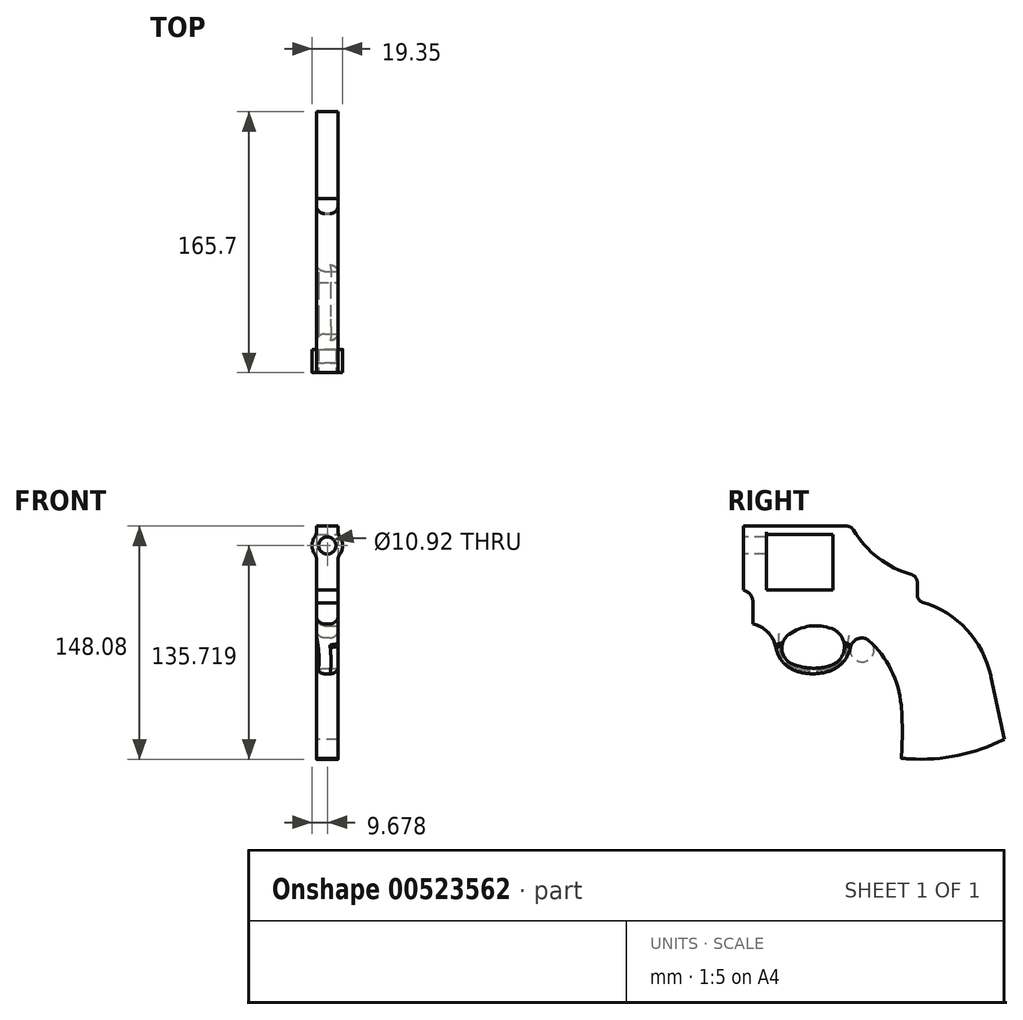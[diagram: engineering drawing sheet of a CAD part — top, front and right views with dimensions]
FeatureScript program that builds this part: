
annotation { "Feature Type Name" : "Feature", "Feature Type Description" : "" }
export const myFeature = defineFeature(function(context is Context, id is Id, definition is map)
    precondition{}
    {
        {
            var Q0;
            Q0=qCreatedBy(makeId("Right.planeOp"),FACE);
            var sketch = newSketch(context, id + "F0", { "sketchPlane" : qUnion([Q0])});
            skLineSegment(sketch, "E0", {"start": v(-44.54, 37.78) * mm, "end": v(-44.54, -2.86) * mm});
            skLineSegment(sketch, "E1", {"start": v(-44.54, 37.78) * mm, "end": v(24.04, 37.78) * mm});
            skLineSegment(sketch, "E2", {"start": v(-51.95, 6.03) * mm, "end": v(65.95, 6.03) * mm, "construction": true});
            skArc(sketch, "E3", {"start": v(24.04, 37.78) * mm, "mid": v(41.55, 17.35) * mm, "end": v(65.95, 6.03) * mm});
            skArc(sketch, "E4", {"start": v(-38.5, -10.9) * mm, "mid": v(-40.03, -5.77) * mm, "end": v(-44.54, -2.86) * mm});
            skLineSegment(sketch, "E5", {"start": v(-38.5, -10.9) * mm, "end": v(-38.5, -24.32) * mm});
            skArc(sketch, "E6", {"start": v(-23.87, -39.34) * mm, "mid": v(-28.94, -29.64) * mm, "end": v(-38.5, -24.32) * mm});
            skArc(sketch, "E7", {"start": v(-23.87, -39.34) * mm, "mid": v(-19.25, -48.7) * mm, "end": v(-10.5, -54.4) * mm});
            skArc(sketch, "E8", {"start": v(-10.5, -54.4) * mm, "mid": v(-0.28, -56) * mm, "end": v(9.93, -54.4) * mm});
            skArc(sketch, "E9", {"start": v(9.93, -54.4) * mm, "mid": v(18.76, -48.7) * mm, "end": v(23.5, -39.34) * mm});
            skArc(sketch, "E10", {"start": v(31.68, -33.31) * mm, "mid": v(26.44, -34.76) * mm, "end": v(23.5, -39.34) * mm});
            skArc(sketch, "E11", {"start": v(35, -34.76) * mm, "mid": v(33.46, -33.77) * mm, "end": v(31.68, -33.31) * mm});
            skPoint(sketch, "E11.startSnap0", {"position": v(26.44, -34.76) * mm});
            skArc(sketch, "E12", {"start": v(112.83, -58.17) * mm, "mid": v(112.72, -57.65) * mm, "end": v(112.6, -57.14) * mm});
            skArc(sketch, "E13", {"start": v(55.75, -109.63) * mm, "mid": v(89.3, -108.4) * mm, "end": v(121.16, -97.73) * mm});
            skArc(sketch, "E14", {"start": v(55.75, -109.63) * mm, "mid": v(56.47, -92.87) * mm, "end": v(55.75, -76.1) * mm});
            skArc(sketch, "E15", {"start": v(55.75, -76.1) * mm, "mid": v(49.34, -53.44) * mm, "end": v(35, -34.76) * mm});
            skLineSegment(sketch, "E16", {"start": v(112.83, -58.17) * mm, "end": v(121.16, -97.73) * mm});
            skLineSegment(sketch, "E17", {"start": v(65.95, 6.03) * mm, "end": v(65.95, -9.62) * mm});
            skArc(sketch, "E18", {"start": v(112.6, -57.14) * mm, "mid": v(96.09, -26.7) * mm, "end": v(65.95, -9.62) * mm});
            skSolve(sketch);
        }
        {
            var Q0;
            Q0 = qSketchRegion(id + "F0", true);
            extrude(context, id + "F1", {"entities" : qUnion([Q0]), "depth" : 13.72 * mm, "offsetDistance" : 25.4 * mm});
        }
        {
            var Q0;
            Q0=makeQuery(id+"F1.opExtrude","CAP_FACE",FACE,{"disambiguationData":[OSD([sQuery(id+"F0.wireOp",EDGE,"E0"),sQuery(id+"F0.wireOp",EDGE,"E1"),sQuery(id+"F0.wireOp",EDGE,"E3"),sQuery(id+"F0.wireOp",EDGE,"E4"),sQuery(id+"F0.wireOp",EDGE,"E5"),sQuery(id+"F0.wireOp",EDGE,"E6"),sQuery(id+"F0.wireOp",EDGE,"E7"),sQuery(id+"F0.wireOp",EDGE,"E8"),sQuery(id+"F0.wireOp",EDGE,"E9"),sQuery(id+"F0.wireOp",EDGE,"E10"),sQuery(id+"F0.wireOp",EDGE,"E11"),sQuery(id+"F0.wireOp",EDGE,"E12"),sQuery(id+"F0.wireOp",EDGE,"E13"),sQuery(id+"F0.wireOp",EDGE,"E14"),sQuery(id+"F0.wireOp",EDGE,"E15"),sQuery(id+"F0.wireOp",EDGE,"E16")])],"isStart":false});
            var sketch = newSketch(context, id + "F2", { "sketchPlane" : qUnion([Q0])});
            skLineSegment(sketch, "E19.bottom", {"start": v(-29.8, 32.52) * mm, "end": v(12.53, 32.52) * mm});
            skLineSegment(sketch, "E19.top", {"start": v(-29.8, -2.9) * mm, "end": v(12.53, -2.9) * mm});
            skLineSegment(sketch, "E19.left", {"start": v(-29.8, 32.52) * mm, "end": v(-29.8, -2.9) * mm});
            skLineSegment(sketch, "E19.right", {"start": v(12.53, 32.52) * mm, "end": v(12.53, -2.9) * mm});
            skSolve(sketch);
        }
        {
            var Q0;
            Q0 = qSketchRegion(id + "F2", true);
            extrude(context, id + "F3", {"entities" : qUnion([Q0]), "operationType" : NewBodyOperationType.REMOVE, "oppositeDirection" : true, "depth" : 25.4 * mm, "offsetDistance" : 25.4 * mm});
        }
        {
            var Q0;
            Q0=makeQuery(id+"F1.opExtrude","SWEPT_FACE",FACE,{"disambiguationData":[OSD([sQuery(id+"F0.wireOp",EDGE,"E0")])]});
            var sketch = newSketch(context, id + "F4", { "sketchPlane" : qUnion([Q0])});
            skLineSegment(sketch, "E20", {"start": v(6.86, 37.78) * mm, "end": v(6.86, 2.4) * mm, "construction": true});
            skPoint(sketch, "E20.endSnap0", {"position": v(6.86, 37.78) * mm});
            skSolve(sketch);
        }
        {
            var Q0;
            {var subQ0=sQuery(id+"F0.wireOp",EDGE,"E0");Q0=makeQuery(id+"F4.imprint","IMPRINT",FACE,{"disambiguationData":[TD([[makeQuery(id+"F4.imprint","IMPRINT",EDGE,{"derivedFrom":makeQuery(id+"F1.opExtrude","CAP_EDGE",EDGE,{"disambiguationData":[OSD([subQ0])],"isStart":true})}),1.0]])]});}
            var sketch = newSketch(context, id + "F5", { "sketchPlane" : qUnion([Q0])});
            skCircle(sketch, "E21", {"center": v(6.86, 25.48) * mm, "radius": 9.68 * mm});
            skSolve(sketch);
        }
        {
            var Q0;
            Q0 = qSketchRegion(id + "F5", true);
            extrude(context, id + "F6", {"entities" : qUnion([Q0]), "operationType" : NewBodyOperationType.ADD, "oppositeDirection" : true, "depth" : 14.73 * mm, "offsetDistance" : 25.4 * mm});
        }
        {
            var Q0;
            Q0=makeQuery(id+"F6.boolean.opBoolean","INTERSECT",EDGE,{"disambiguationData":[OD(0.0)],"derivedFrom":[makeQuery(id+"F1.opExtrude","CAP_FACE",FACE,{"disambiguationData":[OSD([sQuery(id+"F0.wireOp",EDGE,"E0"),sQuery(id+"F0.wireOp",EDGE,"E1"),sQuery(id+"F0.wireOp",EDGE,"E3"),sQuery(id+"F0.wireOp",EDGE,"E4"),sQuery(id+"F0.wireOp",EDGE,"E5"),sQuery(id+"F0.wireOp",EDGE,"E6"),sQuery(id+"F0.wireOp",EDGE,"E7"),sQuery(id+"F0.wireOp",EDGE,"E8"),sQuery(id+"F0.wireOp",EDGE,"E9"),sQuery(id+"F0.wireOp",EDGE,"E10"),sQuery(id+"F0.wireOp",EDGE,"E11"),sQuery(id+"F0.wireOp",EDGE,"E12"),sQuery(id+"F0.wireOp",EDGE,"E13"),sQuery(id+"F0.wireOp",EDGE,"E14"),sQuery(id+"F0.wireOp",EDGE,"E15"),sQuery(id+"F0.wireOp",EDGE,"E16")])],"isStart":false}),makeQuery(id+"F6.opExtrude","SWEPT_FACE",FACE,{"disambiguationData":[OSD([sQuery(id+"F5.wireOp",EDGE,"E21")])]})]});
            var Q1;
            Q1=makeQuery(id+"F6.boolean.opBoolean","INTERSECT",EDGE,{"disambiguationData":[OD(1.0)],"derivedFrom":[makeQuery(id+"F1.opExtrude","CAP_FACE",FACE,{"disambiguationData":[OSD([sQuery(id+"F0.wireOp",EDGE,"E0"),sQuery(id+"F0.wireOp",EDGE,"E1"),sQuery(id+"F0.wireOp",EDGE,"E3"),sQuery(id+"F0.wireOp",EDGE,"E4"),sQuery(id+"F0.wireOp",EDGE,"E5"),sQuery(id+"F0.wireOp",EDGE,"E6"),sQuery(id+"F0.wireOp",EDGE,"E7"),sQuery(id+"F0.wireOp",EDGE,"E8"),sQuery(id+"F0.wireOp",EDGE,"E9"),sQuery(id+"F0.wireOp",EDGE,"E10"),sQuery(id+"F0.wireOp",EDGE,"E11"),sQuery(id+"F0.wireOp",EDGE,"E12"),sQuery(id+"F0.wireOp",EDGE,"E13"),sQuery(id+"F0.wireOp",EDGE,"E14"),sQuery(id+"F0.wireOp",EDGE,"E15"),sQuery(id+"F0.wireOp",EDGE,"E16")])],"isStart":false}),makeQuery(id+"F6.opExtrude","SWEPT_FACE",FACE,{"disambiguationData":[OSD([sQuery(id+"F5.wireOp",EDGE,"E21")])]})]});
            var Q2;
            Q2=makeQuery(id+"F6.boolean.opBoolean","INTERSECT",EDGE,{"disambiguationData":[OD(1.0)],"derivedFrom":[makeQuery(id+"F1.opExtrude","CAP_FACE",FACE,{"disambiguationData":[OSD([sQuery(id+"F0.wireOp",EDGE,"E0"),sQuery(id+"F0.wireOp",EDGE,"E1"),sQuery(id+"F0.wireOp",EDGE,"E3"),sQuery(id+"F0.wireOp",EDGE,"E4"),sQuery(id+"F0.wireOp",EDGE,"E5"),sQuery(id+"F0.wireOp",EDGE,"E6"),sQuery(id+"F0.wireOp",EDGE,"E7"),sQuery(id+"F0.wireOp",EDGE,"E8"),sQuery(id+"F0.wireOp",EDGE,"E9"),sQuery(id+"F0.wireOp",EDGE,"E10"),sQuery(id+"F0.wireOp",EDGE,"E11"),sQuery(id+"F0.wireOp",EDGE,"E12"),sQuery(id+"F0.wireOp",EDGE,"E13"),sQuery(id+"F0.wireOp",EDGE,"E14"),sQuery(id+"F0.wireOp",EDGE,"E15"),sQuery(id+"F0.wireOp",EDGE,"E16")])],"isStart":true}),makeQuery(id+"F6.opExtrude","SWEPT_FACE",FACE,{"disambiguationData":[OSD([sQuery(id+"F5.wireOp",EDGE,"E21")])]})]});
            var Q3;
            Q3=makeQuery(id+"F6.boolean.opBoolean","INTERSECT",EDGE,{"disambiguationData":[OD(0.0)],"derivedFrom":[makeQuery(id+"F1.opExtrude","CAP_FACE",FACE,{"disambiguationData":[OSD([sQuery(id+"F0.wireOp",EDGE,"E0"),sQuery(id+"F0.wireOp",EDGE,"E1"),sQuery(id+"F0.wireOp",EDGE,"E3"),sQuery(id+"F0.wireOp",EDGE,"E4"),sQuery(id+"F0.wireOp",EDGE,"E5"),sQuery(id+"F0.wireOp",EDGE,"E6"),sQuery(id+"F0.wireOp",EDGE,"E7"),sQuery(id+"F0.wireOp",EDGE,"E8"),sQuery(id+"F0.wireOp",EDGE,"E9"),sQuery(id+"F0.wireOp",EDGE,"E10"),sQuery(id+"F0.wireOp",EDGE,"E11"),sQuery(id+"F0.wireOp",EDGE,"E12"),sQuery(id+"F0.wireOp",EDGE,"E13"),sQuery(id+"F0.wireOp",EDGE,"E14"),sQuery(id+"F0.wireOp",EDGE,"E15"),sQuery(id+"F0.wireOp",EDGE,"E16")])],"isStart":true}),makeQuery(id+"F6.opExtrude","SWEPT_FACE",FACE,{"disambiguationData":[OSD([sQuery(id+"F5.wireOp",EDGE,"E21")])]})]});
            fillet(context, id + "F7", {"entities" : qUnion([Q0, Q1, Q2, Q3]), "radius" : 5.08 * mm, "tangentPropagation" : true, "allowEdgeOverflow" : false});
        }
        {
            var Q0;
            {var subQ0=sQuery(id+"F0.wireOp",EDGE,"E0");Q0=makeQuery(id+"F4.imprint","IMPRINT",FACE,{"disambiguationData":[TD([[makeQuery(id+"F4.imprint","IMPRINT",EDGE,{"derivedFrom":makeQuery(id+"F1.opExtrude","CAP_EDGE",EDGE,{"disambiguationData":[OSD([subQ0])],"isStart":true})}),1.0]])]});}
            var sketch = newSketch(context, id + "F8", { "sketchPlane" : qUnion([Q0])});
            skCircle(sketch, "E22", {"center": v(6.86, 25.42) * mm, "radius": 5.46 * mm});
            skSolve(sketch);
        }
        {
            var Q0;
            Q0=makeQuery(id+"F8.imprint","IMPRINT",FACE,{"disambiguationData":[TD([[makeQuery(id+"F8.imprint","IMPRINT",EDGE,{"derivedFrom":sQuery(id+"F8.wireOp",EDGE,"E22")}),1.0]])]});
            extrude(context, id + "F9", {"entities" : qUnion([Q0]), "operationType" : NewBodyOperationType.REMOVE, "oppositeDirection" : true, "depth" : 25.4 * mm, "offsetDistance" : 25.4 * mm});
        }
        {
            var Q0;
            Q0=makeQuery(id+"F1.opExtrude","CAP_FACE",FACE,{"disambiguationData":[OSD([sQuery(id+"F0.wireOp",EDGE,"E0"),sQuery(id+"F0.wireOp",EDGE,"E1"),sQuery(id+"F0.wireOp",EDGE,"E3"),sQuery(id+"F0.wireOp",EDGE,"E4"),sQuery(id+"F0.wireOp",EDGE,"E5"),sQuery(id+"F0.wireOp",EDGE,"E6"),sQuery(id+"F0.wireOp",EDGE,"E7"),sQuery(id+"F0.wireOp",EDGE,"E8"),sQuery(id+"F0.wireOp",EDGE,"E9"),sQuery(id+"F0.wireOp",EDGE,"E10"),sQuery(id+"F0.wireOp",EDGE,"E11"),sQuery(id+"F0.wireOp",EDGE,"E12"),sQuery(id+"F0.wireOp",EDGE,"E13"),sQuery(id+"F0.wireOp",EDGE,"E14"),sQuery(id+"F0.wireOp",EDGE,"E15"),sQuery(id+"F0.wireOp",EDGE,"E16")])],"isStart":false});
            var sketch = newSketch(context, id + "F10", { "sketchPlane" : qUnion([Q0])});
            skArc(sketch, "E23", {"start": v(-15.48, -30.93) * mm, "mid": v(-19.98, -40.9) * mm, "end": v(-13.48, -49.7) * mm});
            skArc(sketch, "E24", {"start": v(11.4, -50.6) * mm, "mid": v(19.72, -39.05) * mm, "end": v(11.65, -27.33) * mm});
            skArc(sketch, "E25", {"start": v(-13.48, -49.7) * mm, "mid": v(-1.12, -52.47) * mm, "end": v(11.4, -50.6) * mm});
            skArc(sketch, "E26", {"start": v(11.65, -27.33) * mm, "mid": v(-2.36, -25.77) * mm, "end": v(-15.48, -30.93) * mm});
            skSolve(sketch);
        }
        {
            var Q0;
            Q0 = qSketchRegion(id + "F10", true);
            extrude(context, id + "F11", {"entities" : qUnion([Q0]), "operationType" : NewBodyOperationType.REMOVE, "oppositeDirection" : true, "depth" : 25.4 * mm, "offsetDistance" : 25.4 * mm});
        }
        {
            var Q0;
            Q0=makeQuery(id+"F1.opExtrude","SWEPT_EDGE",EDGE,{"disambiguationData":[OSD([sQuery(id+"F0.wireOp",EDGE,"E3"),sQuery(id+"F0.wireOp",EDGE,"E17")])]});
            var Q1;
            Q1=makeQuery(id+"F1.opExtrude","SWEPT_EDGE",EDGE,{"disambiguationData":[OSD([sQuery(id+"F0.wireOp",EDGE,"E17"),sQuery(id+"F0.wireOp",EDGE,"E18")])]});
            var Q2;
            Q2=makeQuery(id+"F1.opExtrude","SWEPT_EDGE",EDGE,{"disambiguationData":[OSD([sQuery(id+"F0.wireOp",EDGE,"E1"),sQuery(id+"F0.wireOp",EDGE,"E3")])]});
            fillet(context, id + "F12", {"entities" : qUnion([Q0, Q1, Q2]), "radius" : 5.08 * mm, "tangentPropagation" : true, "allowEdgeOverflow" : false});
        }
        {
            var Q0;
            Q0=makeQuery(id+"F1.opExtrude","CAP_EDGE",EDGE,{"disambiguationData":[OSD([sQuery(id+"F0.wireOp",EDGE,"E6")])],"isStart":false});
            var Q1;
            Q1=makeQuery(id+"F1.opExtrude","CAP_EDGE",EDGE,{"disambiguationData":[OSD([sQuery(id+"F0.wireOp",EDGE,"E7")])],"isStart":true});
            var Q2;
            Q2=makeQuery(id+"F11.boolean.opBoolean","COPY",EDGE,{"derivedFrom":makeQuery(id+"F11.opExtrude","CAP_EDGE",EDGE,{"disambiguationData":[OSD([sQuery(id+"F10.wireOp",EDGE,"E26")])],"isStart":true})});
            var Q3;
            Q3=makeQuery(id+"F11.boolean.opBoolean","INTERSECT",EDGE,{"derivedFrom":[makeQuery(id+"F1.opExtrude","CAP_FACE",FACE,{"disambiguationData":[OSD([sQuery(id+"F0.wireOp",EDGE,"E0"),sQuery(id+"F0.wireOp",EDGE,"E1"),sQuery(id+"F0.wireOp",EDGE,"E3"),sQuery(id+"F0.wireOp",EDGE,"E4"),sQuery(id+"F0.wireOp",EDGE,"E5"),sQuery(id+"F0.wireOp",EDGE,"E6"),sQuery(id+"F0.wireOp",EDGE,"E7"),sQuery(id+"F0.wireOp",EDGE,"E8"),sQuery(id+"F0.wireOp",EDGE,"E9"),sQuery(id+"F0.wireOp",EDGE,"E10"),sQuery(id+"F0.wireOp",EDGE,"E11"),sQuery(id+"F0.wireOp",EDGE,"E12"),sQuery(id+"F0.wireOp",EDGE,"E13"),sQuery(id+"F0.wireOp",EDGE,"E14"),sQuery(id+"F0.wireOp",EDGE,"E15"),sQuery(id+"F0.wireOp",EDGE,"E16"),sQuery(id+"F0.wireOp",EDGE,"E17"),sQuery(id+"F0.wireOp",EDGE,"E18")])],"isStart":true}),makeQuery(id+"F11.opExtrude","SWEPT_FACE",FACE,{"disambiguationData":[OSD([sQuery(id+"F10.wireOp",EDGE,"E26")])]})]});
            fillet(context, id + "F13", {"entities" : qUnion([Q0, Q1, Q2, Q3]), "radius" : 5.08 * mm, "tangentPropagation" : true, "allowEdgeOverflow" : false});
        }
    });
